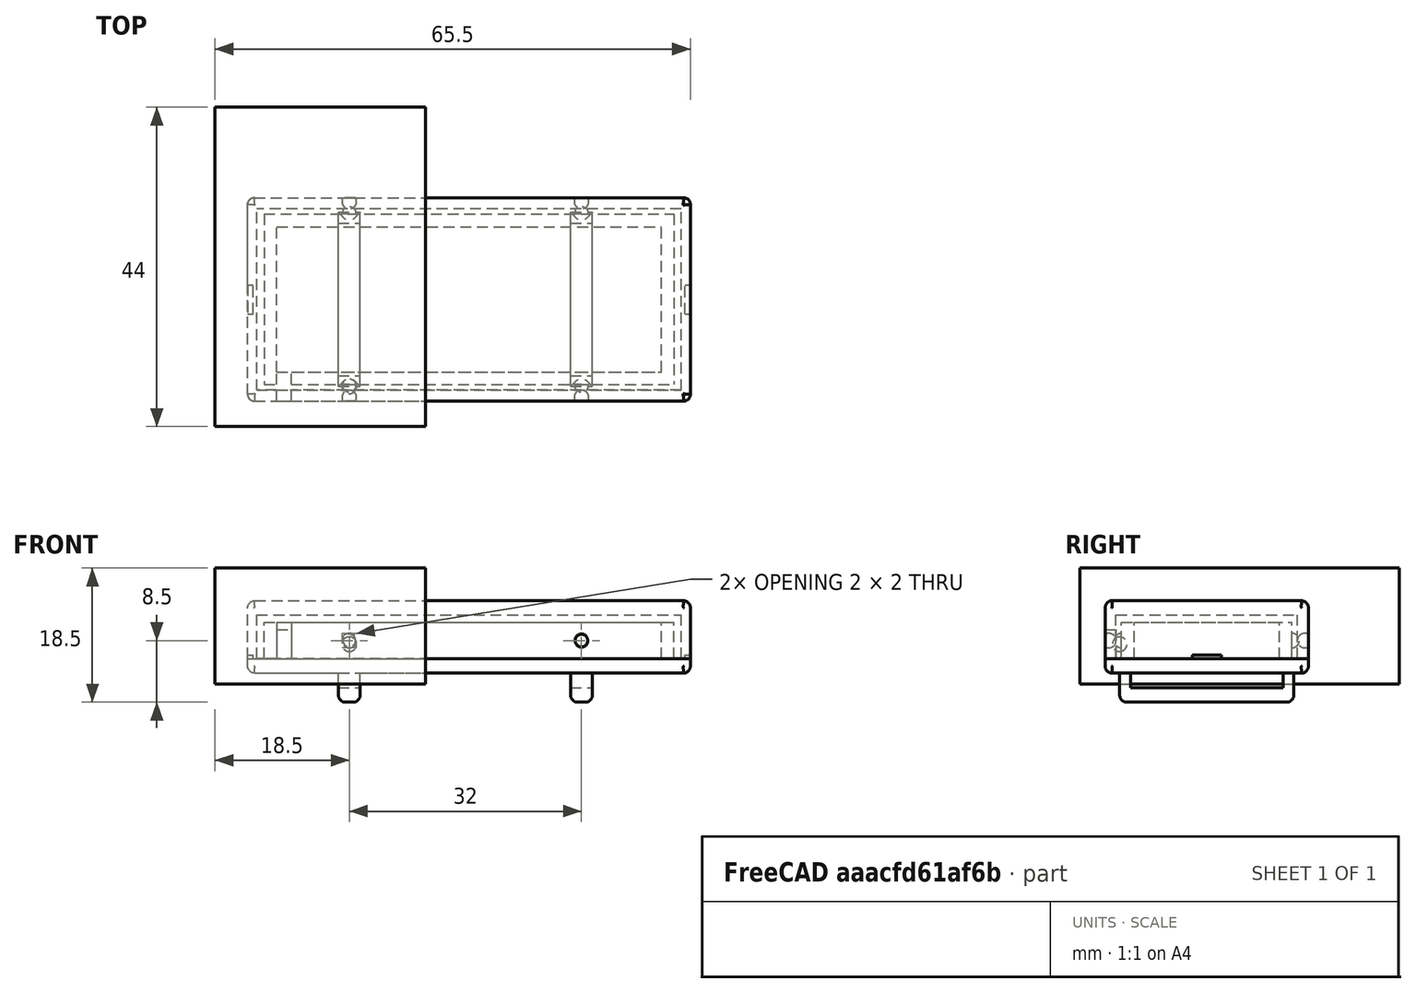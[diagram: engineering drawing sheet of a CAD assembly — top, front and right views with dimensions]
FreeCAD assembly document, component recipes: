
FREECAD ASSEMBLY — COMPONENT RECIPES ("Batteriecasing rev 4")

This assembly document has 9 components, labeled P0..P8 below (a component is one placed body or linked part). 0 of them carry a construction recipe — the FreeCAD feature program that regenerates the part from scratch, quoted from this document or its linked companion documents; the rest are supplied as boundary geometry only. No exploded tour is included for this assembly.
COMPONENT P0 — geometry summary ("Noppel003"; no construction recipe available for this part):
  bounding box: 2.0 x 2.0 x 2.0 mm
  tessellated surface: 8,000 triangles
  volume: 4 mm^3 (52% of its bounding box)
  symmetry: revolution-symmetric about the x axis through its bounding-box center; revolution-symmetric about the y axis through its bounding-box center; revolution-symmetric about the z axis through its bounding-box center; mirror-symmetric across its x mid-plane, y mid-plane, z mid-plane
COMPONENT P1 — geometry summary ("Noppel004"; no construction recipe available for this part):
  bounding box: 2.0 x 2.0 x 2.0 mm
  tessellated surface: 8,000 triangles
  volume: 4 mm^3 (52% of its bounding box)
  symmetry: revolution-symmetric about the x axis through its bounding-box center; revolution-symmetric about the y axis through its bounding-box center; revolution-symmetric about the z axis through its bounding-box center; mirror-symmetric across its x mid-plane, y mid-plane, z mid-plane
COMPONENT P2 — geometry summary ("Noppel005"; no construction recipe available for this part):
  bounding box: 2.0 x 2.0 x 2.0 mm
  tessellated surface: 8,000 triangles
  volume: 4 mm^3 (52% of its bounding box)
  symmetry: revolution-symmetric about the x axis through its bounding-box center; revolution-symmetric about the y axis through its bounding-box center; revolution-symmetric about the z axis through its bounding-box center; mirror-symmetric across its x mid-plane, y mid-plane, z mid-plane
COMPONENT P3 — geometry summary ("Noppel006"; no construction recipe available for this part):
  bounding box: 2.0 x 2.0 x 2.0 mm
  tessellated surface: 8,000 triangles
  volume: 4 mm^3 (52% of its bounding box)
  symmetry: revolution-symmetric about the x axis through its bounding-box center; revolution-symmetric about the y axis through its bounding-box center; revolution-symmetric about the z axis through its bounding-box center; mirror-symmetric across its x mid-plane, y mid-plane, z mid-plane
COMPONENT P4 — geometry summary ("Batterie003"; no construction recipe available for this part):
  bounding box: 53.0 x 20.0 x 5.0 mm
  tessellated surface: 12 triangles
  volume: 5300 mm^3 (100% of its bounding box)
  symmetry: 2-fold rotationally symmetric about the x axis; 2-fold rotationally symmetric about the y axis; mirror-symmetric across its x mid-plane, y mid-plane, z mid-plane
COMPONENT P5 — geometry summary ("Noppel007"; no construction recipe available for this part):
  bounding box: 2.0 x 2.0 x 2.0 mm
  tessellated surface: 8,000 triangles
  volume: 4 mm^3 (52% of its bounding box)
  symmetry: revolution-symmetric about the x axis through its bounding-box center; revolution-symmetric about the y axis through its bounding-box center; revolution-symmetric about the z axis through its bounding-box center; mirror-symmetric across its x mid-plane, y mid-plane, z mid-plane
COMPONENT P6 — geometry summary ("Noppel008"; no construction recipe available for this part):
  bounding box: 2.0 x 2.0 x 2.0 mm
  tessellated surface: 8,000 triangles
  volume: 4 mm^3 (52% of its bounding box)
  symmetry: revolution-symmetric about the x axis through its bounding-box center; revolution-symmetric about the y axis through its bounding-box center; revolution-symmetric about the z axis through its bounding-box center; mirror-symmetric across its x mid-plane, y mid-plane, z mid-plane
COMPONENT P7 — geometry summary ("Noppel009"; no construction recipe available for this part):
  bounding box: 2.0 x 2.0 x 2.0 mm
  tessellated surface: 8,000 triangles
  volume: 4 mm^3 (52% of its bounding box)
  symmetry: revolution-symmetric about the x axis through its bounding-box center; revolution-symmetric about the y axis through its bounding-box center; revolution-symmetric about the z axis through its bounding-box center; mirror-symmetric across its x mid-plane, y mid-plane, z mid-plane
COMPONENT P8 — geometry summary ("Fillet004"; no construction recipe available for this part):
  bounding box: 24.0 x 4.0 x 3.0 mm
  tessellated surface: 322 triangles
  volume: 151 mm^3 (52% of its bounding box)
  symmetry: 2-fold rotationally symmetric about the z axis; mirror-symmetric across its x mid-plane, y mid-plane
PROVENANCE & LICENSES
A FreeCAD (.FCStd) document from a public repository crawl; recipes are the document's own serialized feature recipes (and, for linked parts, companion documents' recipes).
License: as declared in the source repository (recorded in the dataset sidecar).
